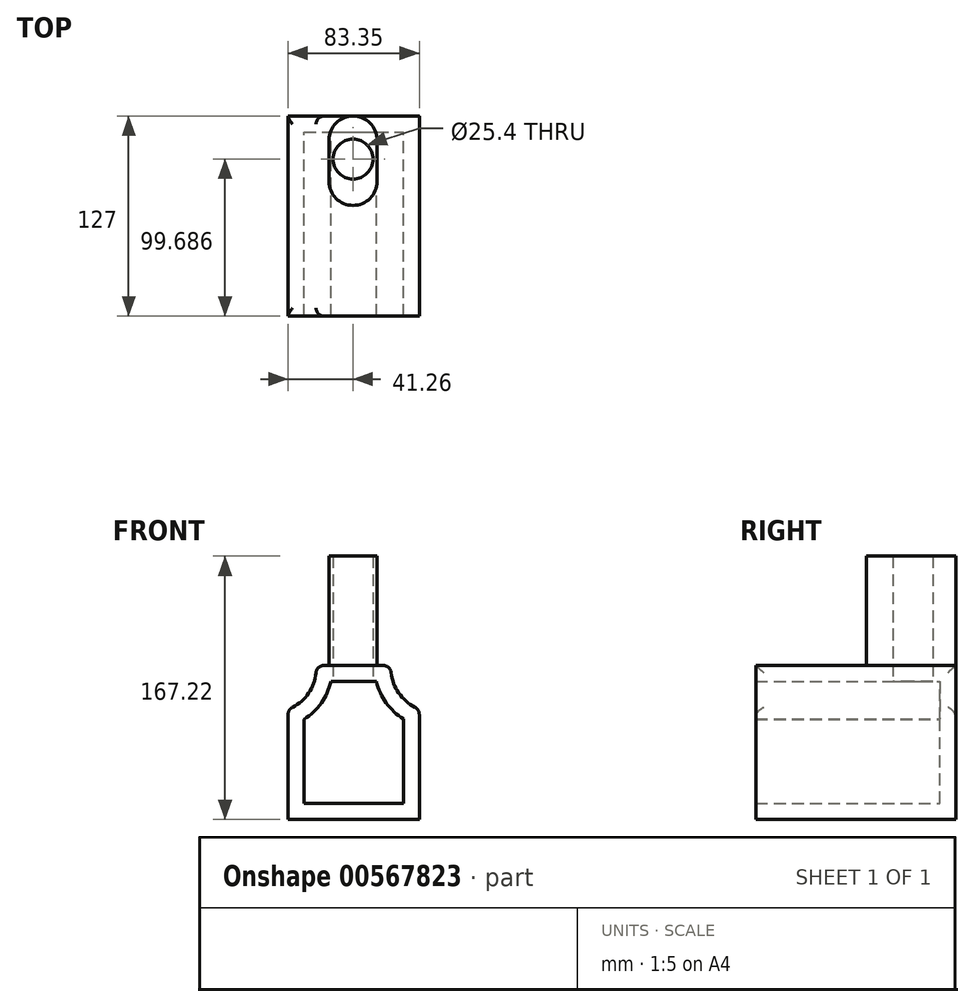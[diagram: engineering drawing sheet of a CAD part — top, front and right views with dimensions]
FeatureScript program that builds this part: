
annotation { "Feature Type Name" : "Feature", "Feature Type Description" : "" }
export const myFeature = defineFeature(function(context is Context, id is Id, definition is map)
    precondition{}
    {
        {
            var Q0;
            Q0=qCreatedBy(makeId("Front.planeOp"),FACE);
            var sketch = newSketch(context, id + "F0", { "sketchPlane" : qUnion([Q0])});
            skLineSegment(sketch, "E0", {"start": v(-41.26, -69.98) * mm, "end": v(42.09, -69.98) * mm});
            skLineSegment(sketch, "E1", {"start": v(42.09, -69.98) * mm, "end": v(42.09, 0) * mm});
            skLineSegment(sketch, "E2", {"start": v(-41.26, -69.98) * mm, "end": v(-41.26, 0) * mm});
            skArc(sketch, "E3", {"start": v(-41.26, 0) * mm, "mid": v(-27.69, 10.9) * mm, "end": v(-23.53, 27.81) * mm});
            skArc(sketch, "E4", {"start": v(42.09, 0) * mm, "mid": v(28.6, 10.99) * mm, "end": v(24.06, 27.79) * mm});
            skLineSegment(sketch, "E5", {"start": v(-23.53, 27.81) * mm, "end": v(24.06, 27.79) * mm});
            skSolve(sketch);
        }
        {
            var Q0;
            Q0 = qSketchRegion(id + "F0", true);
            var Q1;
            Q1=makeQuery(id+"F0.imprint","IMPRINT",FACE,{"disambiguationData":[TD([[makeQuery(id+"F0.imprint","IMPRINT",EDGE,{"derivedFrom":sQuery(id+"F0.wireOp",EDGE,"E0")}),1.0]])]});
            extrude(context, id + "F1", {"entities" : qUnion([Q0, Q1]), "depth" : 127 * mm, "offsetDistance" : 25.4 * mm});
        }
        {
            var Q0;
            Q0=makeQuery(id+"F1.opExtrude","CAP_FACE",FACE,{"disambiguationData":[OSD([sQuery(id+"F0.wireOp",EDGE,"E0"),sQuery(id+"F0.wireOp",EDGE,"E1"),sQuery(id+"F0.wireOp",EDGE,"E2"),sQuery(id+"F0.wireOp",EDGE,"E3"),sQuery(id+"F0.wireOp",EDGE,"E4"),sQuery(id+"F0.wireOp",EDGE,"E5")])],"isStart":false});
            shell(context, id + "F2", {"entities" : qUnion([Q0]), "thickness" : 10.16 * mm});
        }
        {
            var Q0;
            Q0=qCreatedBy(makeId("Top.planeOp"),FACE);
            var sketch = newSketch(context, id + "F3", { "sketchPlane" : qUnion([Q0])});
            skPoint(sketch, "E6", {"position": v(0, -27.31) * mm});
            skSolve(sketch);
        }
        {
            var Q0;
            Q0=sQuery(id+"F3.wireOp",VERTEX,"E6");
            var Q1;
            Q1=makeQuery(id+"F1.opExtrude","SWEPT_BODY",BODY,{"disambiguationData":[OSD([sQuery(id+"F0.wireOp",EDGE,"E0"),sQuery(id+"F0.wireOp",EDGE,"E1"),sQuery(id+"F0.wireOp",EDGE,"E2"),sQuery(id+"F0.wireOp",EDGE,"E3"),sQuery(id+"F0.wireOp",EDGE,"E4"),sQuery(id+"F0.wireOp",EDGE,"E5")])]});
            hole(context, id + "F4", {"style" : HoleStyle.SIMPLE, "endStyle" : HoleEndStyle.THROUGH, "oppositeDirection" : true, "holeDiameter" : 25.4 * mm, "isTappedThrough" : true, "tappedDepth" : 12.7 * mm, "tapClearance" : 3, "locations" : qUnion([Q0]), "scope" : qUnion([Q1])});
        }
        {
            var Q0;
            Q0=qCreatedBy(makeId("Front.planeOp"),FACE);
            var sketch = newSketch(context, id + "F5", { "sketchPlane" : qUnion([Q0])});
            skLineSegment(sketch, "E7.bottom", {"start": v(15.27, 26.36) * mm, "end": v(-15.27, 26.36) * mm});
            skLineSegment(sketch, "E7.top", {"start": v(15.27, 97.24) * mm, "end": v(-15.27, 97.24) * mm});
            skLineSegment(sketch, "E7.left", {"start": v(15.27, 26.36) * mm, "end": v(15.27, 97.24) * mm});
            skLineSegment(sketch, "E7.right", {"start": v(-15.27, 26.36) * mm, "end": v(-15.27, 97.24) * mm});
            skPoint(sketch, "E7.middle", {"position": v(0, 61.8) * mm});
            skSolve(sketch);
        }
        {
            var Q0;
            Q0=makeQuery(id+"F5.imprint","IMPRINT",FACE,{"disambiguationData":[TD([[makeQuery(id+"F5.imprint","IMPRINT",EDGE,{"derivedFrom":sQuery(id+"F5.wireOp",EDGE,"E7.bottom")}),-1.0]])]});
            extrude(context, id + "F6", {"entities" : qUnion([Q0]), "operationType" : NewBodyOperationType.ADD, "depth" : 56.73 * mm, "offsetDistance" : 25.4 * mm});
        }
        {
            var Q0;
            Q0=sQuery(id+"F3.wireOp",VERTEX,"E6");
            var Q1;
            Q1=makeQuery(id+"F1.opExtrude","SWEPT_BODY",BODY,{"disambiguationData":[OSD([sQuery(id+"F0.wireOp",EDGE,"E0"),sQuery(id+"F0.wireOp",EDGE,"E1"),sQuery(id+"F0.wireOp",EDGE,"E2"),sQuery(id+"F0.wireOp",EDGE,"E3"),sQuery(id+"F0.wireOp",EDGE,"E4"),sQuery(id+"F0.wireOp",EDGE,"E5")])]});
            hole(context, id + "F7", {"style" : HoleStyle.SIMPLE, "endStyle" : HoleEndStyle.THROUGH, "oppositeDirection" : true, "holeDiameter" : 25.4 * mm, "isTappedThrough" : true, "tappedDepth" : 12.7 * mm, "tapClearance" : 3, "locations" : qUnion([Q0]), "scope" : qUnion([Q1])});
        }
        {
            var Q0;
            Q0=makeQuery(id+"F6.opExtrude","CAP_EDGE",EDGE,{"disambiguationData":[OSD([sQuery(id+"F5.wireOp",EDGE,"E7.left")])],"isStart":true});
            var Q1;
            Q1=makeQuery(id+"F6.opExtrude","CAP_EDGE",EDGE,{"disambiguationData":[OSD([sQuery(id+"F5.wireOp",EDGE,"E7.right")])],"isStart":true});
            var Q2;
            Q2=makeQuery(id+"F6.opExtrude","CAP_EDGE",EDGE,{"disambiguationData":[OSD([sQuery(id+"F5.wireOp",EDGE,"E7.left")])],"isStart":false});
            var Q3;
            Q3=makeQuery(id+"F6.opExtrude","CAP_EDGE",EDGE,{"disambiguationData":[OSD([sQuery(id+"F5.wireOp",EDGE,"E7.right")])],"isStart":false});
            fillet(context, id + "F8", {"entities" : qUnion([Q0, Q1, Q2, Q3]), "radius" : 15.24 * mm, "allowEdgeOverflow" : false});
        }
        {
            var Q0;
            Q0=makeQuery(id+"F1.opExtrude","SWEPT_EDGE",EDGE,{"disambiguationData":[OSD([sQuery(id+"F0.wireOp",EDGE,"E1"),sQuery(id+"F0.wireOp",EDGE,"E4")])]});
            var Q1;
            Q1=makeQuery(id+"F1.opExtrude","SWEPT_EDGE",EDGE,{"disambiguationData":[OSD([sQuery(id+"F0.wireOp",EDGE,"E4"),sQuery(id+"F0.wireOp",EDGE,"E5")])]});
            var Q2;
            Q2=makeQuery(id+"F1.opExtrude","SWEPT_FACE",FACE,{"disambiguationData":[OSD([sQuery(id+"F0.wireOp",EDGE,"E3")])]});
            fillet(context, id + "F9", {"entities" : qUnion([Q0, Q1, Q2]), "radius" : 5.08 * mm, "tangentPropagation" : true, "allowEdgeOverflow" : false});
        }
    });
